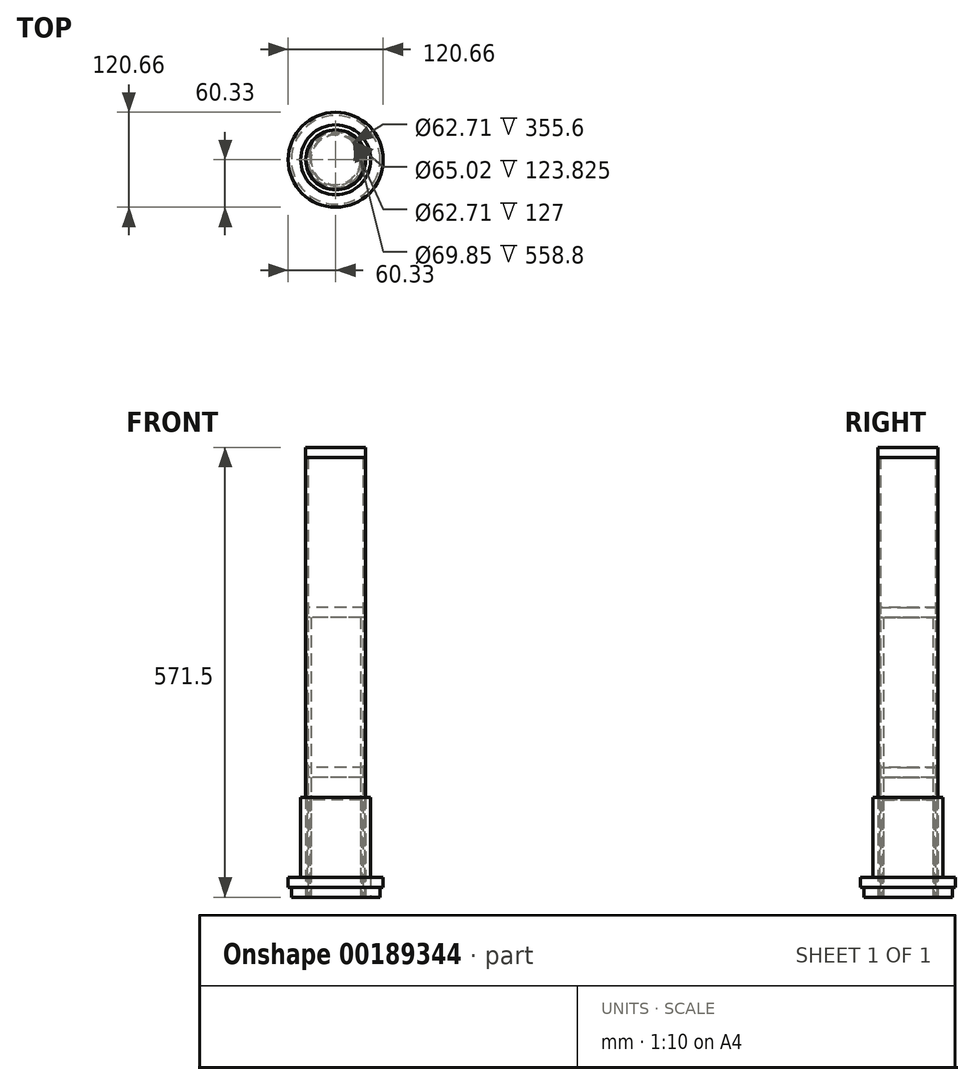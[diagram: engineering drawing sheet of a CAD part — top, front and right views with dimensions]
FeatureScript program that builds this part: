
annotation { "Feature Type Name" : "Feature", "Feature Type Description" : "" }
export const myFeature = defineFeature(function(context is Context, id is Id, definition is map)
    precondition{}
    {
        {
            var Q0;
            Q0=qCreatedBy(makeId("Top.planeOp"),FACE);
            var sketch = newSketch(context, id + "F0", { "sketchPlane" : qUnion([Q0])});
            skCircle(sketch, "E0", {"center": v(0, 0) * mm, "radius": 44.45 * mm});
            skCircle(sketch, "E1", {"center": v(0, 0) * mm, "radius": 32.51 * mm});
            skSolve(sketch);
        }
        {
            var Q0;
            Q0 = qSketchRegion(id + "F0", true);
            extrude(context, id + "F1", {"entities" : qUnion([Q0]), "depth" : 127 * mm});
        }
        {
            var Q0;
            Q0=makeQuery(id+"F1.opExtrude","CAP_EDGE",EDGE,{"disambiguationData":[OSD([sQuery(id+"F0.wireOp",EDGE,"E1")])],"isStart":false});
            chamfer(context, id + "F2", {"entities" : qUnion([Q0]), "width" : 3.17 * mm, "tangentPropagation" : true});
        }
        {
            var Q0;
            Q0=qCreatedBy(makeId("Top.planeOp"),FACE);
            var sketch = newSketch(context, id + "F3", { "sketchPlane" : qUnion([Q0])});
            skCircle(sketch, "E2", {"center": v(0, 0) * mm, "radius": 31.36 * mm});
            skCircle(sketch, "E3", {"center": v(0, 0) * mm, "radius": 36.51 * mm});
            skSolve(sketch);
        }
        {
            var Q0;
            Q0 = qSketchRegion(id + "F3", true);
            extrude(context, id + "F4", {"entities" : qUnion([Q0]), "depth" : 355.6 * mm});
        }
        {
            var Q0;
            Q0=makeQuery(id+"F4.opExtrude","CAP_FACE",FACE,{"disambiguationData":[OSD([sQuery(id+"F3.wireOp",EDGE,"E2"),sQuery(id+"F3.wireOp",EDGE,"E3")])],"isStart":false});
            var sketch = newSketch(context, id + "F5", { "sketchPlane" : qUnion([Q0])});
            skCircle(sketch, "E4.0", {"center": v(0, 0) * mm, "radius": 36.51 * mm});
            skSolve(sketch);
        }
        {
            var Q0;
            Q0 = qSketchRegion(id + "F5", true);
            extrude(context, id + "F6", {"entities" : qUnion([Q0]), "depth" : 12.7 * mm});
        }
        {
            var Q0;
            Q0=qCreatedBy(makeId("Top.planeOp"),FACE);
            var sketch = newSketch(context, id + "F7", { "sketchPlane" : qUnion([Q0])});
            skCircle(sketch, "E5", {"center": v(0, 0) * mm, "radius": 34.93 * mm});
            skCircle(sketch, "E6", {"center": v(0, 0) * mm, "radius": 38.1 * mm});
            skSolve(sketch);
        }
        {
            var Q0;
            Q0 = qSketchRegion(id + "F7", true);
            extrude(context, id + "F8", {"entities" : qUnion([Q0]), "depth" : 558.8 * mm});
        }
        {
            var Q0;
            Q0=makeQuery(id+"F8.opExtrude","CAP_FACE",FACE,{"disambiguationData":[OSD([sQuery(id+"F7.wireOp",EDGE,"E5"),sQuery(id+"F7.wireOp",EDGE,"E6")])],"isStart":false});
            var sketch = newSketch(context, id + "F9", { "sketchPlane" : qUnion([Q0])});
            skCircle(sketch, "E7.0", {"center": v(0, 0) * mm, "radius": 38.1 * mm});
            skSolve(sketch);
        }
        {
            var Q0;
            Q0 = qSketchRegion(id + "F9", true);
            extrude(context, id + "F10", {"entities" : qUnion([Q0]), "depth" : 12.7 * mm});
        }
        {
            var Q0;
            Q0=qCreatedBy(makeId("Right.planeOp"),FACE);
            var sketch = newSketch(context, id + "F11", { "sketchPlane" : qUnion([Q0])});
            skLineSegment(sketch, "E8", {"start": v(0, 0) * mm, "end": v(0, 25.4) * mm, "construction": true});
            skLineSegment(sketch, "E9", {"start": v(0, 25.4) * mm, "end": v(60.32, 25.4) * mm});
            skLineSegment(sketch, "E10", {"start": v(60.32, 25.4) * mm, "end": v(60.32, 12.7) * mm});
            skLineSegment(sketch, "E11", {"start": v(60.33, 12.7) * mm, "end": v(56.32, 12.7) * mm});
            skLineSegment(sketch, "E12", {"start": v(56.32, 12.7) * mm, "end": v(56.32, 0) * mm});
            skLineSegment(sketch, "E13", {"start": v(56.32, 0) * mm, "end": v(0, 0) * mm});
            skLineSegment(sketch, "E14", {"start": v(0, 25.4) * mm, "end": v(0, 0) * mm});
            skSolve(sketch);
        }
        {
            var Q0;
            Q0 = qSketchRegion(id + "F11", true);
            var Q1;
            Q1=sQuery(id+"F11.wireOp",EDGE,"E8");
            revolve(context, id + "F12", {"entities" : qUnion([Q0]), "axis" : qUnion([Q1]), "revolveType" : RevolveType.FULL});
        }
        {
            var Q0;
            Q0=makeQuery(id+"F12.opRevolve","SWEPT_FACE",FACE,{"disambiguationData":[OSD([sQuery(id+"F11.wireOp",EDGE,"E9")])]});
            var sketch = newSketch(context, id + "F13", { "sketchPlane" : qUnion([Q0])});
            skCircle(sketch, "E15", {"center": v(0, 0) * mm, "radius": 31.36 * mm});
            skCircle(sketch, "E16", {"center": v(0, 0) * mm, "radius": 36.51 * mm});
            skSolve(sketch);
        }
        {
            var Q0;
            Q0 = qSketchRegion(id + "F13", true);
            extrude(context, id + "F14", {"entities" : qUnion([Q0]), "depth" : 127 * mm});
        }
        {
            var Q0;
            Q0=makeQuery(id+"F14.opExtrude","CAP_FACE",FACE,{"disambiguationData":[OSD([sQuery(id+"F13.wireOp",EDGE,"E15"),sQuery(id+"F13.wireOp",EDGE,"E16")])],"isStart":false});
            var sketch = newSketch(context, id + "F15", { "sketchPlane" : qUnion([Q0])});
            skCircle(sketch, "E17.0", {"center": v(0, 0) * mm, "radius": 36.51 * mm});
            skSolve(sketch);
        }
        {
            var Q0;
            Q0 = qSketchRegion(id + "F15", true);
            extrude(context, id + "F16", {"entities" : qUnion([Q0]), "depth" : 12.7 * mm});
        }
    });
